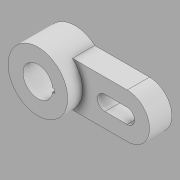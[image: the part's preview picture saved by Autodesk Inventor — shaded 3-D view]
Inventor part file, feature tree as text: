
AUTODESK INVENTOR PART (.ipt)
format: ipt  version: 2020 (Build 240168000, 168)  size: 134,144 bytes
history: native  units: mm
features: extrude x2, sketch x2, other x1
ambient origin geometry x8: Origin, YZ Plane, XZ Plane, XY Plane, X Axis, Y Axis, Z Axis, Center Point
bodies: Body1 (feature_tree)
feature tree (5):
  other  "Sólido1"
  extrude  "Extrusión1"  Depth=40.0mm
  extrude  "Extrusión2"  Depth=20.0mm
  sketch  "Boceto1"  dims[d0=80.0mm d1=40.0mm]
  sketch  "Boceto2"  dims[d3=5.0mm d4=130.0mm d5=60.0mm d7=30.0mm d8=50.0mm d9=20.0mm d10=85.0mm d11=10.0mm d12=10.0mm d13=30.0mm d14=0.0mm d16=5.0mm d18=0.0mm d19=20.0mm d20=0.0mm d15=0.5mm]
